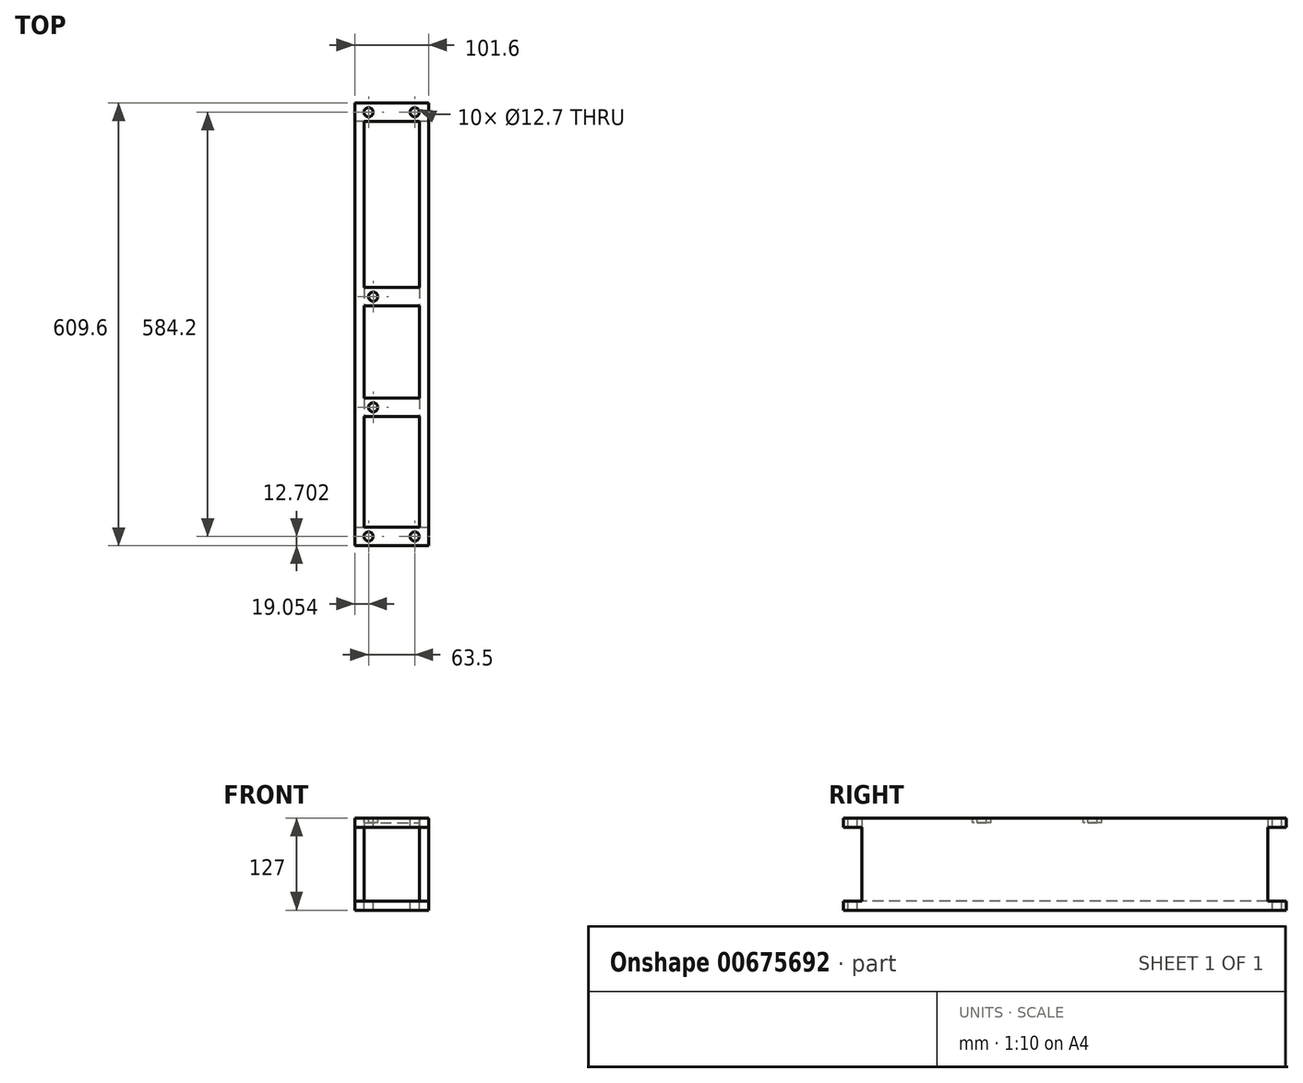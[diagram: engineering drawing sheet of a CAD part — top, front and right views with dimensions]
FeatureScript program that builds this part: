
annotation { "Feature Type Name" : "Feature", "Feature Type Description" : "" }
export const myFeature = defineFeature(function(context is Context, id is Id, definition is map)
    precondition{}
    {
        {
            var Q0;
            Q0=qCreatedBy(makeId("Top.planeOp"),FACE);
            var sketch = newSketch(context, id + "F0", { "sketchPlane" : qUnion([Q0])});
            skLineSegment(sketch, "E0.bottom", {"start": v(-138.95, -277.45) * mm, "end": v(-37.35, -277.45) * mm});
            skLineSegment(sketch, "E0.top", {"start": v(-138.95, 332.15) * mm, "end": v(-37.35, 332.15) * mm});
            skLineSegment(sketch, "E0.left", {"start": v(-138.95, -277.45) * mm, "end": v(-138.95, 332.15) * mm});
            skLineSegment(sketch, "E0.right", {"start": v(-37.35, -277.45) * mm, "end": v(-37.35, 332.15) * mm});
            skLineSegment(sketch, "E1.bottom", {"start": v(-126.25, 306.75) * mm, "end": v(-50.05, 306.75) * mm});
            skLineSegment(sketch, "E1.top", {"start": v(-126.25, -252.05) * mm, "end": v(-50.05, -252.05) * mm});
            skLineSegment(sketch, "E1.left", {"start": v(-126.25, 306.75) * mm, "end": v(-126.25, -252.05) * mm});
            skLineSegment(sketch, "E1.right", {"start": v(-50.05, 306.75) * mm, "end": v(-50.05, -252.05) * mm});
            skSolve(sketch);
        }
        {
            var Q0;
            Q0=makeQuery(id+"F0.imprint","IMPRINT",FACE,{"disambiguationData":[TD([[makeQuery(id+"F0.imprint","IMPRINT",EDGE,{"derivedFrom":sQuery(id+"F0.wireOp",EDGE,"E0.bottom")}),1.0]])]});
            extrude(context, id + "F1", {"entities" : qUnion([Q0]), "depth" : 127 * mm, "offsetDistance" : 25.4 * mm});
        }
        {
            var Q0;
            Q0=makeQuery(id+"F1.opExtrude","CAP_FACE",FACE,{"disambiguationData":[OSD([sQuery(id+"F0.wireOp",EDGE,"E0.bottom"),sQuery(id+"F0.wireOp",EDGE,"E0.top"),sQuery(id+"F0.wireOp",EDGE,"E0.left"),sQuery(id+"F0.wireOp",EDGE,"E0.right"),sQuery(id+"F0.wireOp",EDGE,"E1.bottom"),sQuery(id+"F0.wireOp",EDGE,"E1.top"),sQuery(id+"F0.wireOp",EDGE,"E1.left"),sQuery(id+"F0.wireOp",EDGE,"E1.right")])],"isStart":true});
            var sketch = newSketch(context, id + "F2", { "sketchPlane" : qUnion([Q0])});
            skLineSegment(sketch, "E2.bottom", {"start": v(-126.25, 252.05) * mm, "end": v(-50.05, 252.05) * mm});
            skLineSegment(sketch, "E2.top", {"start": v(-126.25, -306.75) * mm, "end": v(-50.05, -306.75) * mm});
            skLineSegment(sketch, "E2.left", {"start": v(-126.25, 252.05) * mm, "end": v(-126.25, -306.75) * mm});
            skLineSegment(sketch, "E2.right", {"start": v(-50.05, 252.05) * mm, "end": v(-50.05, -306.75) * mm});
            skSolve(sketch);
        }
        {
            var Q0;
            Q0=makeQuery(id+"F2.imprint","IMPRINT",FACE,{"disambiguationData":[TD([[makeQuery(id+"F2.imprint","IMPRINT",EDGE,{"derivedFrom":sQuery(id+"F2.wireOp",EDGE,"E2.bottom")}),-1.0]])]});
            extrude(context, id + "F3", {"entities" : qUnion([Q0]), "operationType" : NewBodyOperationType.ADD, "oppositeDirection" : true, "depth" : 19.05 * mm, "offsetDistance" : 25.4 * mm});
        }
        {
            var Q0;
            Q0=makeQuery(id+"F1.opExtrude","CAP_FACE",FACE,{"disambiguationData":[OSD([sQuery(id+"F0.wireOp",EDGE,"E0.bottom"),sQuery(id+"F0.wireOp",EDGE,"E0.top"),sQuery(id+"F0.wireOp",EDGE,"E0.left"),sQuery(id+"F0.wireOp",EDGE,"E0.right"),sQuery(id+"F0.wireOp",EDGE,"E1.bottom"),sQuery(id+"F0.wireOp",EDGE,"E1.top"),sQuery(id+"F0.wireOp",EDGE,"E1.left"),sQuery(id+"F0.wireOp",EDGE,"E1.right")])],"isStart":false});
            var sketch = newSketch(context, id + "F4", { "sketchPlane" : qUnion([Q0])});
            skLineSegment(sketch, "E3.bottom", {"start": v(-126.25, 78.15) * mm, "end": v(-50.05, 78.15) * mm});
            skLineSegment(sketch, "E3.top", {"start": v(-126.25, 52.75) * mm, "end": v(-50.05, 52.75) * mm});
            skLineSegment(sketch, "E3.left", {"start": v(-126.25, 78.15) * mm, "end": v(-126.25, 52.75) * mm});
            skLineSegment(sketch, "E3.right", {"start": v(-50.05, 78.15) * mm, "end": v(-50.05, 52.75) * mm});
            skLineSegment(sketch, "E4.bottom", {"start": v(-126.25, -74.25) * mm, "end": v(-50.05, -74.25) * mm});
            skLineSegment(sketch, "E4.top", {"start": v(-126.25, -99.65) * mm, "end": v(-50.05, -99.65) * mm});
            skLineSegment(sketch, "E4.left", {"start": v(-126.25, -74.25) * mm, "end": v(-126.25, -99.65) * mm});
            skLineSegment(sketch, "E4.right", {"start": v(-50.05, -74.25) * mm, "end": v(-50.05, -99.65) * mm});
            skSolve(sketch);
        }
        {
            var Q0;
            Q0=makeQuery(id+"F4.imprint","IMPRINT",FACE,{"disambiguationData":[TD([[makeQuery(id+"F4.imprint","IMPRINT",EDGE,{"derivedFrom":sQuery(id+"F4.wireOp",EDGE,"E3.bottom")}),-1.0]])]});
            var Q1;
            Q1=makeQuery(id+"F4.imprint","IMPRINT",FACE,{"disambiguationData":[TD([[makeQuery(id+"F4.imprint","IMPRINT",EDGE,{"derivedFrom":sQuery(id+"F4.wireOp",EDGE,"E4.bottom")}),-1.0]])]});
            extrude(context, id + "F5", {"entities" : qUnion([Q0, Q1]), "operationType" : NewBodyOperationType.ADD, "oppositeDirection" : true, "depth" : 6.35 * mm, "offsetDistance" : 25.4 * mm});
        }
        {
            var Q0;
            Q0=makeQuery(id+"F1.opExtrude","SWEPT_FACE",FACE,{"disambiguationData":[OSD([sQuery(id+"F0.wireOp",EDGE,"E0.bottom")])]});
            var sketch = newSketch(context, id + "F6", { "sketchPlane" : qUnion([Q0])});
            skLineSegment(sketch, "E5.bottom", {"start": v(-138.95, 114.3) * mm, "end": v(-37.35, 114.3) * mm});
            skLineSegment(sketch, "E5.top", {"start": v(-138.95, 12.7) * mm, "end": v(-37.35, 12.7) * mm});
            skLineSegment(sketch, "E5.left", {"start": v(-138.95, 114.3) * mm, "end": v(-138.95, 12.7) * mm});
            skLineSegment(sketch, "E5.right", {"start": v(-37.35, 114.3) * mm, "end": v(-37.35, 12.7) * mm});
            skSolve(sketch);
        }
        {
            var Q0;
            Q0=makeQuery(id+"F6.imprint","IMPRINT",FACE,{"disambiguationData":[TD([[makeQuery(id+"F6.imprint","IMPRINT",EDGE,{"derivedFrom":sQuery(id+"F6.wireOp",EDGE,"E5.bottom")}),-1.0]])]});
            extrude(context, id + "F7", {"entities" : qUnion([Q0]), "operationType" : NewBodyOperationType.REMOVE, "oppositeDirection" : true, "depth" : 25.4 * mm, "offsetDistance" : 25.4 * mm});
        }
        {
            var Q0;
            Q0=makeQuery(id+"F1.opExtrude","SWEPT_FACE",FACE,{"disambiguationData":[OSD([sQuery(id+"F0.wireOp",EDGE,"E0.top")])]});
            var sketch = newSketch(context, id + "F8", { "sketchPlane" : qUnion([Q0])});
            skLineSegment(sketch, "E6.bottom", {"start": v(37.35, 114.3) * mm, "end": v(138.95, 114.3) * mm});
            skLineSegment(sketch, "E6.top", {"start": v(37.35, 12.7) * mm, "end": v(138.95, 12.7) * mm});
            skLineSegment(sketch, "E6.left", {"start": v(37.35, 114.3) * mm, "end": v(37.35, 12.7) * mm});
            skLineSegment(sketch, "E6.right", {"start": v(138.95, 114.3) * mm, "end": v(138.95, 12.7) * mm});
            skSolve(sketch);
        }
        {
            var Q0;
            Q0=makeQuery(id+"F8.imprint","IMPRINT",FACE,{"disambiguationData":[TD([[makeQuery(id+"F8.imprint","IMPRINT",EDGE,{"derivedFrom":sQuery(id+"F8.wireOp",EDGE,"E6.bottom")}),-1.0]])]});
            extrude(context, id + "F9", {"entities" : qUnion([Q0]), "operationType" : NewBodyOperationType.REMOVE, "oppositeDirection" : true, "depth" : 25.4 * mm, "offsetDistance" : 25.4 * mm});
        }
        {
            var Q0;
            Q0=makeQuery(id+"F3.opExtrude","CAP_FACE",FACE,{"disambiguationData":[OSD([sQuery(id+"F2.wireOp",EDGE,"E2.bottom"),sQuery(id+"F2.wireOp",EDGE,"E2.top"),sQuery(id+"F2.wireOp",EDGE,"E2.left"),sQuery(id+"F2.wireOp",EDGE,"E2.right")])],"isStart":false});
            extrude(context, id + "F10", {"entities" : qUnion([Q0]), "operationType" : NewBodyOperationType.REMOVE, "oppositeDirection" : true, "depth" : 6.35 * mm, "offsetDistance" : 25.4 * mm});
        }
        {
            var Q0;
            Q0=makeQuery(id+"F5.boolean.opBoolean","MERGE",FACE,{"derivedFrom":[makeQuery(id+"F1.opExtrude","CAP_FACE",FACE,{"disambiguationData":[OSD([sQuery(id+"F0.wireOp",EDGE,"E0.bottom"),sQuery(id+"F0.wireOp",EDGE,"E0.top"),sQuery(id+"F0.wireOp",EDGE,"E0.left"),sQuery(id+"F0.wireOp",EDGE,"E0.right"),sQuery(id+"F0.wireOp",EDGE,"E1.bottom"),sQuery(id+"F0.wireOp",EDGE,"E1.top"),sQuery(id+"F0.wireOp",EDGE,"E1.left"),sQuery(id+"F0.wireOp",EDGE,"E1.right")])],"isStart":false}),makeQuery(id+"F5.opExtrude","CAP_FACE",FACE,{"disambiguationData":[OSD([sQuery(id+"F4.wireOp",EDGE,"E3.bottom"),sQuery(id+"F4.wireOp",EDGE,"E3.top"),sQuery(id+"F4.wireOp",EDGE,"E3.left"),sQuery(id+"F4.wireOp",EDGE,"E3.right")])],"isStart":true}),makeQuery(id+"F5.opExtrude","CAP_FACE",FACE,{"disambiguationData":[OSD([sQuery(id+"F4.wireOp",EDGE,"E4.bottom"),sQuery(id+"F4.wireOp",EDGE,"E4.top"),sQuery(id+"F4.wireOp",EDGE,"E4.left"),sQuery(id+"F4.wireOp",EDGE,"E4.right")])],"isStart":true})]});
            var sketch = newSketch(context, id + "F11", { "sketchPlane" : qUnion([Q0])});
            skCircle(sketch, "E7", {"center": v(-113.55, 65.45) * mm, "radius": 6.35 * mm});
            skCircle(sketch, "E8", {"center": v(-113.55, -86.95) * mm, "radius": 6.35 * mm});
            skSolve(sketch);
        }
        {
            var Q0;
            Q0=makeQuery(id+"F11.imprint","IMPRINT",FACE,{"disambiguationData":[TD([[makeQuery(id+"F11.imprint","IMPRINT",EDGE,{"derivedFrom":sQuery(id+"F11.wireOp",EDGE,"E7")}),1.0]])]});
            var Q1;
            Q1=makeQuery(id+"F11.imprint","IMPRINT",FACE,{"disambiguationData":[TD([[makeQuery(id+"F11.imprint","IMPRINT",EDGE,{"derivedFrom":sQuery(id+"F11.wireOp",EDGE,"E8")}),1.0]])]});
            extrude(context, id + "F12", {"entities" : qUnion([Q0, Q1]), "operationType" : NewBodyOperationType.REMOVE, "oppositeDirection" : true, "depth" : 6.35 * mm, "offsetDistance" : 25.4 * mm});
        }
        {
            var Q0;
            Q0=makeQuery(id+"F5.boolean.opBoolean","MERGE",FACE,{"derivedFrom":[makeQuery(id+"F1.opExtrude","CAP_FACE",FACE,{"disambiguationData":[OSD([sQuery(id+"F0.wireOp",EDGE,"E0.bottom"),sQuery(id+"F0.wireOp",EDGE,"E0.top"),sQuery(id+"F0.wireOp",EDGE,"E0.left"),sQuery(id+"F0.wireOp",EDGE,"E0.right"),sQuery(id+"F0.wireOp",EDGE,"E1.bottom"),sQuery(id+"F0.wireOp",EDGE,"E1.top"),sQuery(id+"F0.wireOp",EDGE,"E1.left"),sQuery(id+"F0.wireOp",EDGE,"E1.right")])],"isStart":false}),makeQuery(id+"F5.opExtrude","CAP_FACE",FACE,{"disambiguationData":[OSD([sQuery(id+"F4.wireOp",EDGE,"E3.bottom"),sQuery(id+"F4.wireOp",EDGE,"E3.top"),sQuery(id+"F4.wireOp",EDGE,"E3.left"),sQuery(id+"F4.wireOp",EDGE,"E3.right")])],"isStart":true}),makeQuery(id+"F5.opExtrude","CAP_FACE",FACE,{"disambiguationData":[OSD([sQuery(id+"F4.wireOp",EDGE,"E4.bottom"),sQuery(id+"F4.wireOp",EDGE,"E4.top"),sQuery(id+"F4.wireOp",EDGE,"E4.left"),sQuery(id+"F4.wireOp",EDGE,"E4.right")])],"isStart":true})]});
            var sketch = newSketch(context, id + "F13", { "sketchPlane" : qUnion([Q0])});
            skCircle(sketch, "E9", {"center": v(-119.9, 319.45) * mm, "radius": 6.35 * mm});
            skCircle(sketch, "E10", {"center": v(-56.4, 319.45) * mm, "radius": 6.35 * mm});
            skCircle(sketch, "E11", {"center": v(-119.9, -264.75) * mm, "radius": 6.35 * mm});
            skCircle(sketch, "E12", {"center": v(-56.4, -264.75) * mm, "radius": 6.35 * mm});
            skSolve(sketch);
        }
        {
            var Q0;
            Q0=makeQuery(id+"F13.imprint","IMPRINT",FACE,{"disambiguationData":[TD([[makeQuery(id+"F13.imprint","IMPRINT",EDGE,{"derivedFrom":sQuery(id+"F13.wireOp",EDGE,"E11")}),1.0]])]});
            var Q1;
            Q1=makeQuery(id+"F13.imprint","IMPRINT",FACE,{"disambiguationData":[TD([[makeQuery(id+"F13.imprint","IMPRINT",EDGE,{"derivedFrom":sQuery(id+"F13.wireOp",EDGE,"E12")}),1.0]])]});
            var Q2;
            Q2=makeQuery(id+"F13.imprint","IMPRINT",FACE,{"disambiguationData":[TD([[makeQuery(id+"F13.imprint","IMPRINT",EDGE,{"derivedFrom":sQuery(id+"F13.wireOp",EDGE,"E9")}),1.0]])]});
            var Q3;
            Q3=makeQuery(id+"F13.imprint","IMPRINT",FACE,{"disambiguationData":[TD([[makeQuery(id+"F13.imprint","IMPRINT",EDGE,{"derivedFrom":sQuery(id+"F13.wireOp",EDGE,"E10")}),1.0]])]});
            extrude(context, id + "F14", {"entities" : qUnion([Q0, Q1, Q2, Q3]), "operationType" : NewBodyOperationType.REMOVE, "oppositeDirection" : true, "depth" : 12.7 * mm, "offsetDistance" : 25.4 * mm});
        }
        {
            var Q0;
            Q0=makeQuery(id+"F13.imprint","IMPRINT",FACE,{"disambiguationData":[TD([[makeQuery(id+"F13.imprint","IMPRINT",EDGE,{"derivedFrom":sQuery(id+"F13.wireOp",EDGE,"E9")}),1.0]])]});
            var Q1;
            Q1=makeQuery(id+"F13.imprint","IMPRINT",FACE,{"disambiguationData":[TD([[makeQuery(id+"F13.imprint","IMPRINT",EDGE,{"derivedFrom":sQuery(id+"F13.wireOp",EDGE,"E10")}),1.0]])]});
            var Q2;
            Q2=makeQuery(id+"F13.imprint","IMPRINT",FACE,{"disambiguationData":[TD([[makeQuery(id+"F13.imprint","IMPRINT",EDGE,{"derivedFrom":sQuery(id+"F13.wireOp",EDGE,"E11")}),1.0]])]});
            var Q3;
            Q3=makeQuery(id+"F13.imprint","IMPRINT",FACE,{"disambiguationData":[TD([[makeQuery(id+"F13.imprint","IMPRINT",EDGE,{"derivedFrom":sQuery(id+"F13.wireOp",EDGE,"E12")}),1.0]])]});
            extrude(context, id + "F15", {"entities" : qUnion([Q0, Q1, Q2, Q3]), "operationType" : NewBodyOperationType.REMOVE, "oppositeDirection" : true, "depth" : 127 * mm, "offsetDistance" : 25.4 * mm});
        }
    });
